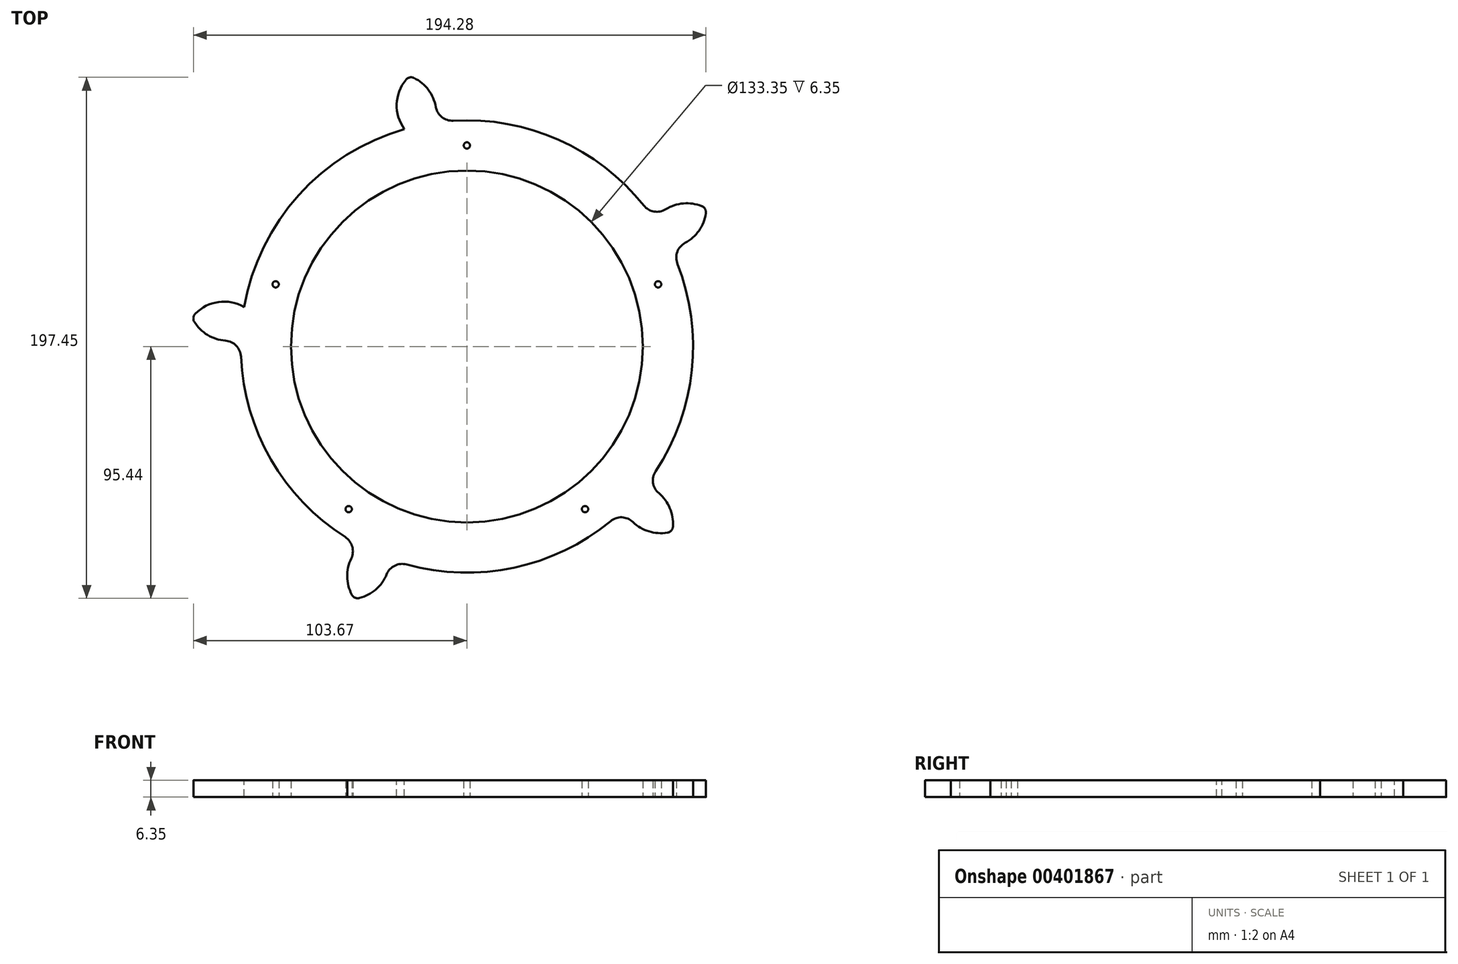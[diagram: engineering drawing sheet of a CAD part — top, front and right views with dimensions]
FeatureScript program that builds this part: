
annotation { "Feature Type Name" : "Feature", "Feature Type Description" : "" }
export const myFeature = defineFeature(function(context is Context, id is Id, definition is map)
    precondition{}
    {
        {
            var Q0;
            Q0=qCreatedBy(makeId("Top.planeOp"),FACE);
            var sketch = newSketch(context, id + "F0", { "sketchPlane" : qUnion([Q0])});
            skCircle(sketch, "E0", {"center": v(0, 0) * mm, "radius": 85.73 * mm});
            skCircle(sketch, "E1", {"center": v(0, 0) * mm, "radius": 66.68 * mm});
            skCircle(sketch, "E2", {"center": v(0, 0) * mm, "radius": 76.2 * mm, "construction": true});
            skLineSegment(sketch, "E3", {"start": v(0, 0) * mm, "end": v(0, 76.2) * mm, "construction": true});
            skCircle(sketch, "E4", {"center": v(0, 76.2) * mm, "radius": 1.2 * mm});
            skCircle(sketch, "E5.1.0", {"center": v(-72.47, 23.55) * mm, "radius": 1.2 * mm});
            skCircle(sketch, "E5.2.0", {"center": v(-44.79, -61.65) * mm, "radius": 1.2 * mm});
            skCircle(sketch, "E5.3.0", {"center": v(44.79, -61.65) * mm, "radius": 1.2 * mm});
            skCircle(sketch, "E5.4.0", {"center": v(72.47, 23.55) * mm, "radius": 1.2 * mm});
            skSolve(sketch);
        }
        {
            var Q0;
            Q0=qSketchRegion(id+"F0",true);
            extrude(context, id + "F1", {"entities" : qUnion([Q0]), "depth" : 6.35 * mm});
        }
        {
            var Q0;
            Q0=makeQuery(id+"F1.opExtrude","CAP_FACE",FACE,{"disambiguationData":[OSD([sQuery(id+"F0.wireOp",EDGE,"E0"),sQuery(id+"F0.wireOp",EDGE,"E1"),sQuery(id+"F0.wireOp",EDGE,"E4"),sQuery(id+"F0.wireOp",EDGE,"E5.1.0"),sQuery(id+"F0.wireOp",EDGE,"E5.2.0"),sQuery(id+"F0.wireOp",EDGE,"E5.3.0"),sQuery(id+"F0.wireOp",EDGE,"E5.4.0")])],"isStart":false});
            var sketch = newSketch(context, id + "F2", { "sketchPlane" : qUnion([Q0])});
            skLineSegment(sketch, "E6", {"start": v(0, 0) * mm, "end": v(0, 85.73) * mm, "construction": true});
            skLineSegment(sketch, "E7", {"start": v(0, 0) * mm, "end": v(-17.82, 83.85) * mm, "construction": true});
            skLineSegment(sketch, "E8", {"start": v(-17.82, 83.85) * mm, "end": v(-21.78, 102.49) * mm, "construction": true});
            skArc(sketch, "E9", {"start": v(-21.78, 102.49) * mm, "mid": v(-26.54, 92.8) * mm, "end": v(-23.68, 82.39) * mm});
            skArc(sketch, "E10", {"start": v(-11.87, 84.9) * mm, "mid": v(-13.5, 95.57) * mm, "end": v(-21.78, 102.49) * mm});
            skArc(sketch, "E11", {"start": v(-23.68, 82.39) * mm, "mid": v(-17.82, 83.85) * mm, "end": v(-11.87, 84.9) * mm});
            skArc(sketch, "E12.1.0", {"start": v(-85.67, 2.94) * mm, "mid": v(-85.26, 8.96) * mm, "end": v(-84.41, 14.94) * mm});
            skArc(sketch, "E12.1.1", {"start": v(-104.2, 10.95) * mm, "mid": v(-96.46, 3.44) * mm, "end": v(-85.67, 2.94) * mm});
            skArc(sketch, "E12.1.2", {"start": v(-84.41, 14.94) * mm, "mid": v(-95.06, 16.7) * mm, "end": v(-104.2, 10.95) * mm});
            skArc(sketch, "E12.2.0", {"start": v(-29.27, -80.57) * mm, "mid": v(-34.87, -78.31) * mm, "end": v(-40.3, -75.66) * mm});
            skArc(sketch, "E12.2.1", {"start": v(-42.62, -95.72) * mm, "mid": v(-33.07, -90.67) * mm, "end": v(-29.27, -80.57) * mm});
            skArc(sketch, "E12.2.2", {"start": v(-40.3, -75.66) * mm, "mid": v(-45.25, -85.25) * mm, "end": v(-42.62, -95.72) * mm});
            skArc(sketch, "E12.3.0", {"start": v(67.59, -52.73) * mm, "mid": v(63.7, -57.36) * mm, "end": v(59.5, -61.7) * mm});
            skArc(sketch, "E12.3.1", {"start": v(77.86, -70.1) * mm, "mid": v(76.01, -59.48) * mm, "end": v(67.59, -52.73) * mm});
            skArc(sketch, "E12.3.2", {"start": v(59.5, -61.7) * mm, "mid": v(67.1, -69.38) * mm, "end": v(77.86, -70.1) * mm});
            skArc(sketch, "E12.4.0", {"start": v(71.04, 47.98) * mm, "mid": v(74.24, 42.86) * mm, "end": v(77.07, 37.53) * mm});
            skArc(sketch, "E12.4.1", {"start": v(90.74, 52.39) * mm, "mid": v(80.05, 53.91) * mm, "end": v(71.04, 47.98) * mm});
            skArc(sketch, "E12.4.2", {"start": v(77.07, 37.53) * mm, "mid": v(86.72, 42.37) * mm, "end": v(90.74, 52.39) * mm});
            skSolve(sketch);
        }
        {
            var Q0;
            Q0 = qSketchRegion(id + "F2", true);
            var Q1;
            Q1=makeQuery(id+"F1.opExtrude","CAP_FACE",FACE,{"disambiguationData":[OSD([sQuery(id+"F0.wireOp",EDGE,"E0"),sQuery(id+"F0.wireOp",EDGE,"E1"),sQuery(id+"F0.wireOp",EDGE,"E4"),sQuery(id+"F0.wireOp",EDGE,"E5.1.0"),sQuery(id+"F0.wireOp",EDGE,"E5.2.0"),sQuery(id+"F0.wireOp",EDGE,"E5.3.0"),sQuery(id+"F0.wireOp",EDGE,"E5.4.0")])],"isStart":true});
            extrude(context, id + "F3", {"entities" : qUnion([Q0]), "operationType" : NewBodyOperationType.ADD, "endBound" : BoundingType.UP_TO_SURFACE, "oppositeDirection" : true, "endBoundEntityFace" : qUnion([Q1]), "depth" : 25.4 * mm});
        }
        {
            var Q0;
            Q0=makeQuery(id+"F3.opExtrude","SWEPT_EDGE",EDGE,{"disambiguationData":[OSD([sQuery(id+"F0.wireOp",EDGE,"E0"),sQuery(id+"F2.wireOp",EDGE,"E10"),sQuery(id+"F2.wireOp",EDGE,"E11")])]});
            var Q1;
            Q1=makeQuery(id+"F3.opExtrude","SWEPT_EDGE",EDGE,{"disambiguationData":[OSD([sQuery(id+"F0.wireOp",EDGE,"E0"),sQuery(id+"F2.wireOp",EDGE,"E9"),sQuery(id+"F2.wireOp",EDGE,"E11")])]});
            var Q2;
            Q2=makeQuery(id+"F3.opExtrude","SWEPT_EDGE",EDGE,{"disambiguationData":[OSD([sQuery(id+"F0.wireOp",EDGE,"E0"),sQuery(id+"F2.wireOp",EDGE,"E12.4.0"),sQuery(id+"F2.wireOp",EDGE,"E12.4.1")])]});
            var Q3;
            Q3=makeQuery(id+"F3.opExtrude","SWEPT_EDGE",EDGE,{"disambiguationData":[OSD([sQuery(id+"F0.wireOp",EDGE,"E0"),sQuery(id+"F2.wireOp",EDGE,"E12.4.0"),sQuery(id+"F2.wireOp",EDGE,"E12.4.2")])]});
            var Q4;
            Q4=makeQuery(id+"F3.opExtrude","SWEPT_EDGE",EDGE,{"disambiguationData":[OSD([sQuery(id+"F0.wireOp",EDGE,"E0"),sQuery(id+"F2.wireOp",EDGE,"E12.3.0"),sQuery(id+"F2.wireOp",EDGE,"E12.3.1")])]});
            var Q5;
            Q5=makeQuery(id+"F3.opExtrude","SWEPT_EDGE",EDGE,{"disambiguationData":[OSD([sQuery(id+"F0.wireOp",EDGE,"E0"),sQuery(id+"F2.wireOp",EDGE,"E12.3.0"),sQuery(id+"F2.wireOp",EDGE,"E12.3.2")])]});
            var Q6;
            Q6=makeQuery(id+"F3.opExtrude","SWEPT_EDGE",EDGE,{"disambiguationData":[OSD([sQuery(id+"F0.wireOp",EDGE,"E0"),sQuery(id+"F2.wireOp",EDGE,"E12.2.0"),sQuery(id+"F2.wireOp",EDGE,"E12.2.1")])]});
            var Q7;
            Q7=makeQuery(id+"F3.opExtrude","SWEPT_EDGE",EDGE,{"disambiguationData":[OSD([sQuery(id+"F0.wireOp",EDGE,"E0"),sQuery(id+"F2.wireOp",EDGE,"E12.2.0"),sQuery(id+"F2.wireOp",EDGE,"E12.2.2")])]});
            var Q8;
            Q8=makeQuery(id+"F3.opExtrude","SWEPT_EDGE",EDGE,{"disambiguationData":[OSD([sQuery(id+"F0.wireOp",EDGE,"E0"),sQuery(id+"F2.wireOp",EDGE,"E12.1.0"),sQuery(id+"F2.wireOp",EDGE,"E12.1.1")])]});
            var Q9;
            Q9=makeQuery(id+"F3.opExtrude","SWEPT_EDGE",EDGE,{"disambiguationData":[OSD([sQuery(id+"F0.wireOp",EDGE,"E0"),sQuery(id+"F2.wireOp",EDGE,"E12.1.0"),sQuery(id+"F2.wireOp",EDGE,"E12.1.2")])]});
            fillet(context, id + "F4", {"entities" : qUnion([Q0, Q1, Q2, Q3, Q4, Q5, Q6, Q7, Q8, Q9]), "radius" : 6.35 * mm, "tangentPropagation" : true, "allowEdgeOverflow" : false});
        }
        {
            var Q0;
            Q0=makeQuery(id+"F3.opExtrude","SWEPT_EDGE",EDGE,{"disambiguationData":[OSD([sQuery(id+"F2.wireOp",EDGE,"E12.3.1"),sQuery(id+"F2.wireOp",EDGE,"E12.3.2")])]});
            var Q1;
            Q1=makeQuery(id+"F3.opExtrude","SWEPT_EDGE",EDGE,{"disambiguationData":[OSD([sQuery(id+"F2.wireOp",EDGE,"E12.2.1"),sQuery(id+"F2.wireOp",EDGE,"E12.2.2")])]});
            var Q2;
            Q2=makeQuery(id+"F3.opExtrude","SWEPT_EDGE",EDGE,{"disambiguationData":[OSD([sQuery(id+"F2.wireOp",EDGE,"E12.1.1"),sQuery(id+"F2.wireOp",EDGE,"E12.1.2")])]});
            var Q3;
            Q3=makeQuery(id+"F3.opExtrude","SWEPT_EDGE",EDGE,{"disambiguationData":[OSD([sQuery(id+"F2.wireOp",EDGE,"E9"),sQuery(id+"F2.wireOp",EDGE,"E10")])]});
            var Q4;
            Q4=makeQuery(id+"F3.opExtrude","SWEPT_EDGE",EDGE,{"disambiguationData":[OSD([sQuery(id+"F2.wireOp",EDGE,"E12.4.1"),sQuery(id+"F2.wireOp",EDGE,"E12.4.2")])]});
            fillet(context, id + "F5", {"entities" : qUnion([Q0, Q1, Q2, Q3, Q4]), "radius" : 2.54 * mm, "tangentPropagation" : true, "allowEdgeOverflow" : false});
        }
    });
